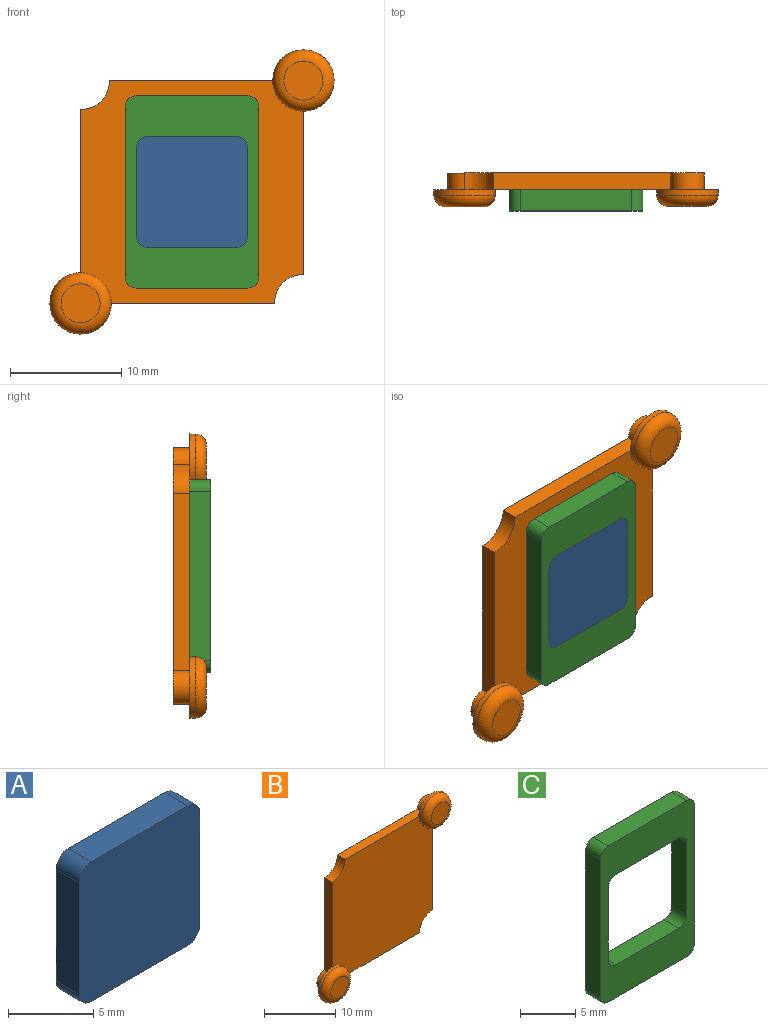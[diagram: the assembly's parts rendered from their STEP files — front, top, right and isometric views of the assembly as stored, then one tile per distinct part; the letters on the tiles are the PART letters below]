
ASSEMBLY  parts=3 mates=2
PART A: 10 faces, bbox 10x1.9x10 mm
  f0: plane 8x1.9mm, normal (1,0,0), area 15.2mm2, adj f1,f7,f8,f9
  f1: cylinder r=1mm len=1.9mm, axis (0,1,0), area 3mm2, adj f0,f2,f8,f9
  f2: plane 8x1.9mm, normal (0,0,1), area 15.2mm2, adj f1,f3,f8,f9
  f3: cylinder r=1mm len=1.9mm, axis (0,1,0), area 3mm2, adj f2,f4,f8,f9
  f4: plane 8x1.9mm, normal (-1,0,0), area 15.2mm2, adj f3,f5,f8,f9
  f5: cylinder r=1mm len=1.9mm, axis (0,1,0), area 3mm2, adj f4,f6,f8,f9
  f6: plane 8x1.9mm, normal (0,0,-1), area 15.2mm2, adj f5,f7,f8,f9
  f7: cylinder r=1mm len=1.9mm, axis (0,1,0), area 3mm2, adj f0,f6,f8,f9
  f8: plane 10x10mm, normal (0,-1,0), area 99.1mm2, adj f0,f1,f2,f3,f4,f5,f6,f7
  f9: plane 10x10mm, normal (0,1,0), area 99.1mm2, adj f0,f1,f2,f3,f4,f5,f6,f7
PART B: 18 faces, bbox 26x3x26 mm
  f0: plane 20x20mm, normal (0,-1,0), area 377.5mm2, adj f1,f3,f4,f5,f7,f8,f12,f15
  f1: plane 15.9x1.5mm, normal (1,0,0), area 23.8mm2, adj f0,f2,f8,f9,f10
  f2: cylinder r=1.5mm len=3mm, axis (0,1,0), area 10.6mm2, adj f1,f3,f9,f10
  f3: plane 15.9x1.5mm, normal (0,0,1), area 23.9mm2, adj f0,f2,f4,f9,f10
  f4: cylinder r=2.6mm len=2.6mm, axis (0,1,0), area 6.1mm2, adj f0,f3,f5,f9
  f5: plane 15.9x1.5mm, normal (-1,0,0), area 23.8mm2, adj f0,f4,f6,f9,f13
  f6: cylinder r=1.5mm len=3mm, axis (0,1,0), area 10.6mm2, adj f5,f7,f9,f13
  f7: plane 15.9x1.5mm, normal (0,0,-1), area 23.9mm2, adj f0,f6,f8,f9,f13
  f8: cylinder r=2.6mm len=2.6mm, axis (0,1,0), area 6.1mm2, adj f0,f1,f7,f9
  f9: plane 23x23mm, normal (0,1,0), area 400mm2, adj f1,f2,f3,f4,f5,f6,f7,f8
  f10: plane 5.5x5.5mm, normal (0,1,0), area 12.5mm2, adj f1,f2,f3,f12
  f11: plane 3.5x3.5mm, normal (0,-1,0), area 9.6mm2, adj f17
  f12: cylinder r=2.75mm len=5.5mm, axis (0,1,0), area 8.6mm2, adj f0,f10,f17
  f13: plane 5.5x5.5mm, normal (0,1,0), area 12.5mm2, adj f5,f6,f7,f15
  f14: plane 3.5x3.5mm, normal (0,-1,0), area 9.6mm2, adj f16
  f15: cylinder r=2.75mm len=5.5mm, axis (0,1,0), area 8.6mm2, adj f0,f13,f16
  f16: torus R=1.75mm, axis (0,-1,0), area 23.6mm2, adj f14,f15
  f17: torus R=1.75mm, axis (0,-1,0), area 23.6mm2, adj f11,f12
PART C: 18 faces, bbox 12x1.9x17.3 mm
  f0: plane 15.25x1.9mm, normal (1,0,0), area 29mm2, adj f1,f15,f16,f17
  f1: cylinder r=1mm len=1.9mm, axis (0,1,0), area 3mm2, adj f0,f2,f16,f17
  f2: plane 10x1.9mm, normal (0,0,1), area 19mm2, adj f1,f3,f16,f17
  f3: cylinder r=1mm len=1.9mm, axis (0,1,0), area 3mm2, adj f2,f4,f16,f17
  f4: plane 15.25x1.9mm, normal (-1,0,0), area 29mm2, adj f3,f5,f16,f17
  f5: cylinder r=1mm len=1.9mm, axis (0,1,0), area 3mm2, adj f4,f6,f16,f17
  f6: plane 10x1.9mm, normal (0,0,-1), area 19mm2, adj f5,f15,f16,f17
  f7: cylinder r=1mm len=1.9mm, axis (0,1,0), area 3mm2, adj f8,f14,f16,f17
  f8: plane 8x1.9mm, normal (-1,0,0), area 15.2mm2, adj f7,f9,f16,f17
  f9: cylinder r=1mm len=1.9mm, axis (0,1,0), area 3mm2, adj f8,f10,f16,f17
  f10: plane 8x1.9mm, normal (0,0,1), area 15.2mm2, adj f9,f11,f16,f17
  f11: cylinder r=1mm len=1.9mm, axis (0,1,0), area 3mm2, adj f10,f12,f16,f17
  f12: plane 8x1.9mm, normal (1,0,0), area 15.2mm2, adj f11,f13,f16,f17
  f13: cylinder r=1mm len=1.9mm, axis (0,1,0), area 3mm2, adj f12,f14,f16,f17
  f14: plane 8x1.9mm, normal (0,0,-1), area 15.2mm2, adj f7,f13,f16,f17
  f15: cylinder r=1mm len=1.9mm, axis (0,1,0), area 3mm2, adj f0,f6,f16,f17
  f16: plane 17.25x12mm, normal (0,-1,0), area 107mm2, adj f0,f1,f2,f3,f4,f5,f6,f7
  f17: plane 17.25x12mm, normal (0,1,0), area 107mm2, adj f0,f1,f2,f3,f4,f5,f6,f7
PLACE A t=(8.73,5.22,18.25)mm
PLACE B t=(8.73,6.72,18.25)mm
PLACE C t=(8.73,5.22,18.25)mm
MATE fastened B.f0 <-> A.f9  axis (0,-1,0) through (8.73,5.22,31.75)mm
MATE fastened B.f0 <-> C.f17  axis (0,-1,0) through (8.73,5.22,31.75)mm
